# Revit family: IS_Connect_E7139_BIM_DE
name_source: partatom
category: Plumbing Fixtures
revit_build: Autodesk Revit MEP 2014 (Build: 20130308_1515(x64)
units: mm (PartAtom-declared; Revit-internal decimal feet)

## types (6) — shared parameters
Accessories = www.idealstandard.de\ersatzteile
AreaUnits = millimeters
Assembly Code = C1030200
AssetType = Fixed
Brand = Ideal Standard
CodePerformance = DIN EN 14688 CL 10, DIN EN 31
ConnectionType = Plumbing
Default Elevation = 850 mm  [stored 2.78871 ft]
DrainSize = 42 mm  [stored 0.137795 ft]
DurationUnit = year
ExpectedLife = 25
Features = Connect Cube 55cm washbasin, 1 taphole with overflow
GrossWeight = 0
IfcExportAs = IfcSanitaryType
IfcExportType = WASHHANDBASIN
InstallationInstructions = www.idealstandard.de\produkte
LinearUnits = millimeters
ManufacturerURL = www.idealstandard.de
Material = Vitreous china
NBSDescription = Pedestal wash basins
NBSReference = 45-35-70/365
NettWeight = 17,302 kg
NominalHeight = 174 mm
NominalLength = 460 mm
NominalWidth = 550 mm
ProductInformation = www.idealstandard.de\produkte
Shape = Sculptured
Size = 550x460x175mm
Space = Internal
URL = www.idealstandard.com
Uniclass2015Code = Pr_40_20_96_63
Uniclass2015Title = Pedestal wash basins
Uniclass2015Version = Products v1.1
Version = 1
VolumeUnits = Litres
WarrantyDescription = Manufacturers Warranty
WarrantyDurationUnit = year
WashHandBasinMounting = i.e.Wall Hung
WashHandBasinType = Hand Rinse
zero-valued in all types: CWFU, Cost, HWFU, WFU

## per-type parameters (varying)
| type | BIMObjectName | BarCode | Color | Description | E7112 | E7113 | E7114 | Finish | Model | ModelNumber | ModelReference | Name |
| E7139MA Connect Cube 55cm washbasin, 1 taphole with overflow, with Ideal Plus (E7113) | ISI_IdealStandard_PedestalWashBasins_ConnectCube_E7139MA | 5017830399773 | white with ideal plus | E7139MA Connect Cube 55cm washbasin, 1 taphole with overflow | No | Yes | No | white with ideal plus | E7139MA | E7139MA | E7139MA Connect Cube 55cm washbasin, 1 taphole with overflow | PedestalWashBasins_ConnectCube_E7139MA_IdealStandard |
| E7139MA Connect Cube 55cm washbasin, 1 taphole with overflow, with Ideal Plus (E7112) | ISI_IdealStandard_PedestalWashBasins_ConnectCube_E7139MA | 5017830399773 | white with ideal plus | E7139MA Connect Cube 55cm washbasin, 1 taphole with overflow | Yes | No | No | white with ideal plus | E7139MA | E7139MA | E7139MA Connect Cube 55cm washbasin, 1 taphole with overflow | PedestalWashBasins_ConnectCube_E7139MA_IdealStandard |
| E7139MA Connect Cube 55cm washbasin, 1 taphole with overflow, with Ideal Plus (E7114) | ISI_IdealStandard_PedestalWashBasins_ConnectCube_E7139MA | 5017830399773 | white with ideal plus | E7139MA Connect Cube 55cm washbasin, 1 taphole with overflow | No | No | Yes | white with ideal plus | E7139MA | E7139MA | E7139MA Connect Cube 55cm washbasin, 1 taphole with overflow | PedestalWashBasins_ConnectCube_E7139MA_IdealStandard |
| E713901 Connect Cube 55cm washbasin, 1 taphole with overflow (E7112) | ISI_IdealStandard_PedestalWashBasins_ConnectCube_E713901 | 5017830399780 | white | E713901 Connect Cube 55cm washbasin, 1 taphole with overflow | Yes | No | No | white | E713901 | E713901 | E713901 Connect Cube 55cm washbasin, 1 taphole with overflow | PedestalWashBasins_ConnectCube_E713901_IdealStandard |
| E713901 Connect Cube 55cm washbasin, 1 taphole with overflow (E7114) | ISI_IdealStandard_PedestalWashBasins_ConnectCube_E713901 | 5017830399780 | white | E713901 Connect Cube 55cm washbasin, 1 taphole with overflow | No | No | Yes | white | E713901 | E713901 | E713901 Connect Cube 55cm washbasin, 1 taphole with overflow | PedestalWashBasins_ConnectCube_E713901_IdealStandard |
| E713901 Connect Cube 55cm washbasin, 1 taphole with overflow (E7113) | ISI_IdealStandard_PedestalWashBasins_ConnectCube_E713901 | 5017830399780 | white | E713901 Connect Cube 55cm washbasin, 1 taphole with overflow | No | Yes | No | white | E713901 | E713901 | E713901 Connect Cube 55cm washbasin, 1 taphole with overflow | PedestalWashBasins_ConnectCube_E713901_IdealStandard |

note: [stored X ft] marks values corroborated as IEEE doubles in the binary element streams (Revit-internal decimal feet)

## geometry (parser evidence)
native form markers: Sweep x6
no freeform markers — native parametric forms only
